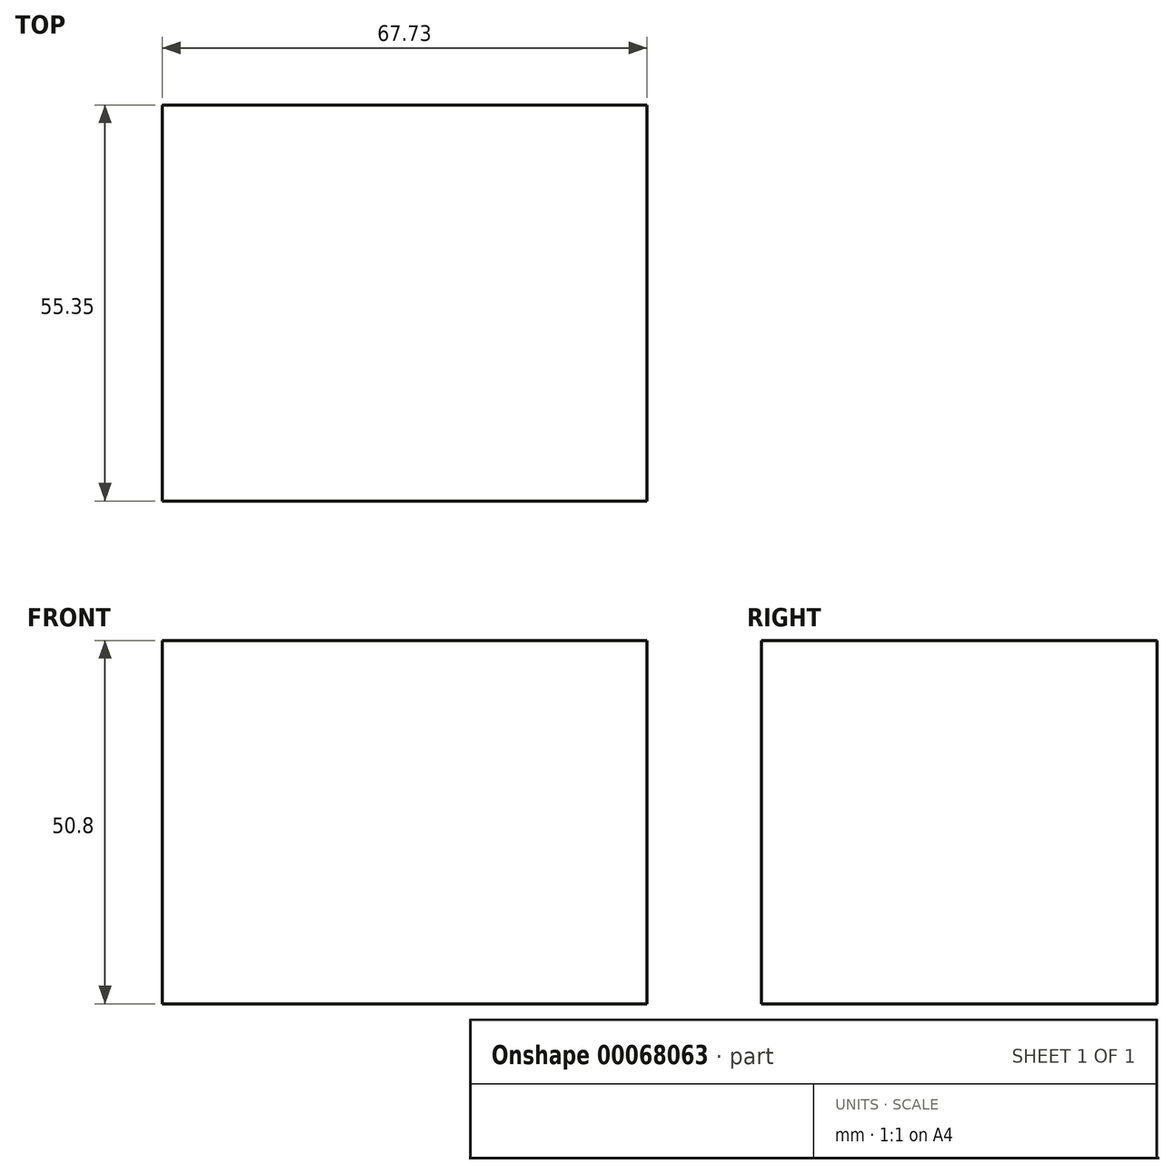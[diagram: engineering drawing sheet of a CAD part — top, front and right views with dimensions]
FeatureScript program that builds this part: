
annotation { "Feature Type Name" : "Feature", "Feature Type Description" : "" }
export const myFeature = defineFeature(function(context is Context, id is Id, definition is map)
    precondition{}
    {
        {
            var Q0;
            Q0=qCreatedBy(makeId("Top.planeOp"),FACE);
            var sketch = newSketch(context, id + "F0", { "sketchPlane" : qUnion([Q0])});
            skLineSegment(sketch, "E0", {"start": v(-31.78, -28.48) * mm, "end": v(-31.78, 26.87) * mm});
            skLineSegment(sketch, "E1", {"start": v(-31.78, 26.87) * mm, "end": v(35.95, 26.87) * mm});
            skLineSegment(sketch, "E2", {"start": v(35.95, 26.87) * mm, "end": v(35.95, -28.48) * mm});
            skLineSegment(sketch, "E3", {"start": v(35.95, -28.48) * mm, "end": v(-31.78, -28.48) * mm});
            skSolve(sketch);
        }
        {
            var Q0;
            Q0=makeQuery(id+"F0.imprint","IMPRINT",FACE,{"disambiguationData":[TD([[makeQuery(id+"F0.imprint","IMPRINT",EDGE,{"derivedFrom":sQuery(id+"F0.wireOp",EDGE,"E0")}),-1.0]])]});
            extrude(context, id + "F1", {"entities" : qUnion([Q0]), "depth" : 50.8 * mm});
        }
    });
